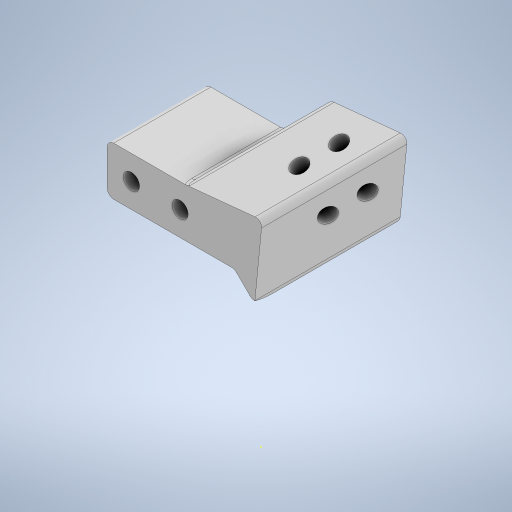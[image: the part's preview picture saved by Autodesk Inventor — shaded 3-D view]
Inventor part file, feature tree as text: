
AUTODESK INVENTOR PART (.ipt)
format: ipt  version: 2024.3 (Build 283343000, 343)  size: 417,280 bytes
history: native  units: mm
features: sketch x14, extrude x10, projected_geometry x7, hole x3, other x1, fillet x1
ambient origin geometry x8: Origin, YZ Plane, XZ Plane, XY Plane, X Axis, Y Axis, Z Axis, Center Point
bodies: Body1 (feature_tree)
feature tree (36):
  other  "ソリッド1"
  extrude  "押し出し1"  Depth=60.0mm
  hole  "穴1"  [1 undecoded]
  extrude  "押し出し2"  Depth=30.0mm TaperAngle=0.0deg
  extrude  "押し出し11"  Depth=7.5mm
  extrude  "押し出し12"  Depth=7.5mm
  extrude  "押し出し17"  Depth=10.5mm
  extrude  "押し出し18"  Depth=10.5mm
  sketch  "スケッチ27"
  extrude  "押し出し19"  Depth=15.0mm
  hole  "穴4"  [1 undecoded]
  hole  "穴5"  [1 undecoded]
  extrude  "押し出し20"  Depth=26.0mm
  fillet  "フィレット1"  Radius=7.5mm
  extrude  "押し出し21"  Depth=7.5mm
  extrude  "押し出し22"  Depth=7.5mm
  sketch  "スケッチ1"
  sketch  "スケッチ2"
  sketch  "スケッチ3"
  projected_geometry  "投影ループ1"
  sketch  "スケッチ15"
  projected_geometry  "投影ループ10"
  sketch  "スケッチ16"
  projected_geometry  "投影ループ11"
  sketch  "スケッチ25"
  projected_geometry  "投影ループ18"
  sketch  "スケッチ26"
  projected_geometry  "投影ループ19"
  sketch  "スケッチ28"
  sketch  "スケッチ29"
  sketch  "スケッチ30"
  sketch  "スケッチ31"
  projected_geometry  "投影ループ20"
  sketch  "スケッチ32"
  projected_geometry  "投影ループ21"
  sketch  "スケッチ33"
note: 3 required parameter values undecoded (feature->parameter linkage not recoverable at this tier; creation-order binding heuristic only, values carry confidence <= 0.55)
